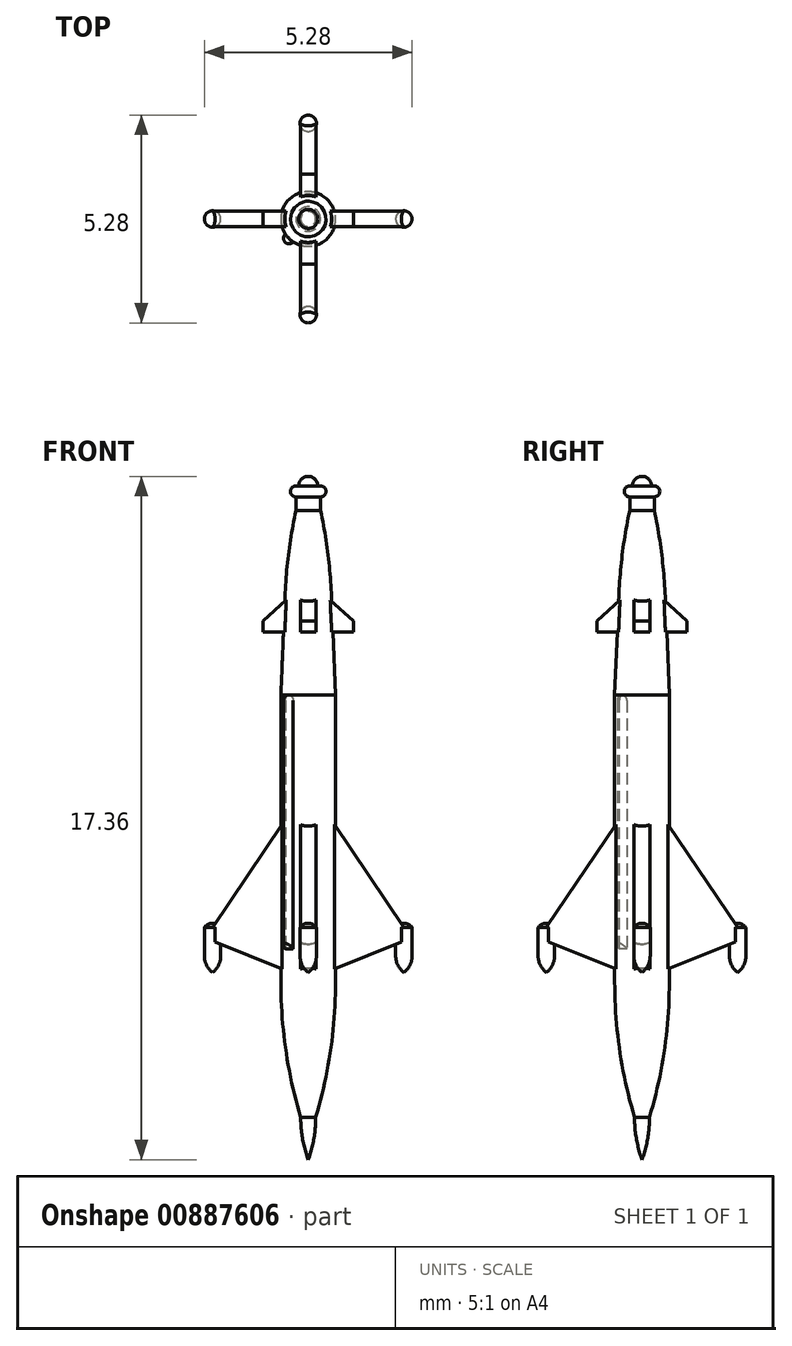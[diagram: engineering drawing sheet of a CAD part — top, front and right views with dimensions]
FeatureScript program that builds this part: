
annotation { "Feature Type Name" : "Feature", "Feature Type Description" : "" }
export const myFeature = defineFeature(function(context is Context, id is Id, definition is map)
    precondition{}
    {
        {
            assignVariable(context, id + "F0", {"name" : "s", "anyValue" : 144});
        }
        {
            var Q0;
            Q0=qCreatedBy(makeId("Front.planeOp"),FACE);
            var sketch = newSketch(context, id + "F1", { "sketchPlane" : qUnion([Q0])});
            skLineSegment(sketch, "E0", {"start": v(0, 0) * mm, "end": v(0, 17.36) * mm});
            skLineSegment(sketch, "E1", {"start": v(0.7, 11.8) * mm, "end": v(0.7, 0) * mm});
            skLineSegment(sketch, "E2", {"start": v(0.7, 0) * mm, "end": v(0, 0) * mm});
            skArc(sketch, "E3", {"start": v(0, 0) * mm, "mid": v(0.14, 0.53) * mm, "end": v(0.2, 1.08) * mm});
            skArc(sketch, "E4", {"start": v(0.2, 1.08) * mm, "mid": v(0.57, 2.78) * mm, "end": v(0.7, 4.51) * mm});
            skLineSegment(sketch, "E5", {"start": v(0.2, 1.08) * mm, "end": v(0.2, 2.11) * mm, "construction": true});
            skArc(sketch, "E6", {"start": v(0.24, 17.12) * mm, "mid": v(0.17, 17.29) * mm, "end": v(0, 17.36) * mm});
            skLineSegment(sketch, "E7", {"start": v(0.24, 17.12) * mm, "end": v(0.31, 17.12) * mm});
            skLineSegment(sketch, "E8", {"start": v(0.31, 16.84) * mm, "end": v(0.31, 16.84) * mm});
            skLineSegment(sketch, "E9", {"start": v(0.31, 16.84) * mm, "end": v(0.31, 16.5) * mm});
            skArc(sketch, "E10", {"start": v(0.31, 16.84) * mm, "mid": v(0.45, 16.98) * mm, "end": v(0.31, 17.12) * mm});
            skLineSegment(sketch, "E11", {"start": v(0.7, 11.8) * mm, "end": v(0.6, 14.3) * mm});
            skArc(sketch, "E12", {"start": v(0.6, 14.3) * mm, "mid": v(0.5, 15.4) * mm, "end": v(0.31, 16.5) * mm});
            skSolve(sketch);
        }
        {
            var Q0;
            {var subQ0=sQuery(id+"F1.wireOp",EDGE,"mrwio9nY-PsAZ-Zbfy-NhIU-sYq0QVbgGXAG");Q0=makeQuery(id+"F1.imprint","IMPRINT",FACE,{"disambiguationData":[TD([[makeQuery(id+"F1.imprint","IMPRINT",EDGE,{"derivedFrom":subQ0}),-1.0]])]});}
            var Q1;
            {var subQ7=sQuery(id+"F1.wireOp",EDGE,"E0");Q1=makeQuery(id+"F1.imprint","IMPRINT",FACE,{"disambiguationData":[TD([[makeQuery(id+"F1.imprint","IMPRINT",EDGE,{"derivedFrom":subQ7}),-1.0]])]});}
            var Q2;
            Q2=sQuery(id+"F1.wireOp",EDGE,"E0");
            revolve(context, id + "F2", {"surfaceOperationType" : NewSurfaceOperationType.NEW, "entities" : qUnion([Q0, Q1]), "axis" : qUnion([Q2]), "revolveType" : RevolveType.FULL});
        }
        {
            var Q0;
            Q0=qCreatedBy(makeId("Front.planeOp"),FACE);
            var sketch = newSketch(context, id + "F3", { "sketchPlane" : qUnion([Q0])});
            skLineSegment(sketch, "E13", {"start": v(0, 0) * mm, "end": v(0, 14.74) * mm});
            skLineSegment(sketch, "E14", {"start": v(0.4, 13.4) * mm, "end": v(0.4, 8.9) * mm});
            skLineSegment(sketch, "E15", {"start": v(0.4, 8.9) * mm, "end": v(2.43, 5.9) * mm});
            skLineSegment(sketch, "E16", {"start": v(0.7, 0) * mm, "end": v(0.7, 32.87) * mm, "construction": true});
            skPoint(sketch, "E17", {"position": v(0.7, 8.47) * mm});
            skLineSegment(sketch, "E18", {"start": v(0.4, 13.4) * mm, "end": v(1.15, 13.4) * mm});
            skLineSegment(sketch, "E19", {"start": v(1.15, 13.4) * mm, "end": v(1.15, 13.68) * mm});
            skLineSegment(sketch, "E20", {"start": v(1.15, 13.68) * mm, "end": v(0, 14.74) * mm});
            skPoint(sketch, "E21", {"position": v(0.7, 13.4) * mm});
            skPoint(sketch, "E22", {"position": v(0.7, 14.1) * mm});
            skLineSegment(sketch, "E23.0", {"start": v(0.7, 4.51) * mm, "end": v(-0.7, 4.51) * mm});
            skLineSegment(sketch, "E24", {"start": v(0, 4.58) * mm, "end": v(2.43, 5.56) * mm});
            skLineSegment(sketch, "E25", {"start": v(2.43, 5.56) * mm, "end": v(2.43, 5.9) * mm});
            skPoint(sketch, "E26", {"position": v(0.7, 4.86) * mm});
            skSolve(sketch);
        }
        {
            var Q0;
            Q0=qSketchRegion(id+"F3",true);
            extrude(context, id + "F4", {"entities" : qUnion([Q0]), "operationType" : NewBodyOperationType.ADD, "depth" : .4 * mm, "offsetDistance" : 25 * mm, "symmetric" : true});
        }
        {
            var Q0;
            Q0=qCreatedBy(makeId("Front.planeOp"),FACE);
            var sketch = newSketch(context, id + "F5", { "sketchPlane" : qUnion([Q0])});
            skLineSegment(sketch, "E27", {"start": v(2.43, 4.76) * mm, "end": v(2.43, 6) * mm});
            skLineSegment(sketch, "E28", {"start": v(2.64, 5.9) * mm, "end": v(2.64, 5.17) * mm});
            skArc(sketch, "E29", {"start": v(2.64, 5.9) * mm, "mid": v(2.55, 5.98) * mm, "end": v(2.43, 6) * mm});
            skArc(sketch, "E30", {"start": v(2.43, 4.76) * mm, "mid": v(2.58, 4.94) * mm, "end": v(2.64, 5.17) * mm});
            skLineSegment(sketch, "E31.0", {"start": v(0.67, 8.52) * mm, "end": v(2.43, 5.9) * mm});
            skSolve(sketch);
        }
        {
            var Q0;
            Q0 = qSketchRegion(id + "F5", true);
            var Q1;
            Q1=sQuery(id+"F5.wireOp",EDGE,"E27");
            revolve(context, id + "F6", {"operationType" : NewBodyOperationType.ADD, "surfaceOperationType" : NewSurfaceOperationType.NEW, "entities" : qUnion([Q0]), "axis" : qUnion([Q1]), "revolveType" : RevolveType.FULL});
        }
        {
            var Q0;
            Q0=makeQuery(id+"F2.opRevolve","SWEPT_BODY",BODY,{"disambiguationData":[OSD([sQuery(id+"F1.wireOp",EDGE,"E0"),sQuery(id+"F1.wireOp",EDGE,"E1"),sQuery(id+"F1.wireOp",EDGE,"E2"),sQuery(id+"F1.wireOp",EDGE,"2EiOItwe-9FNA-eY8p-DkXH-AMy5AHyUmzZA"),sQuery(id+"F1.wireOp",EDGE,"lF35QjYl-MEgV-fRWE-0Yr6-Bt5vS8A7brRf")])]});
            var Q1;
            Q1=makeQuery(id+"F2.opRevolve","SWEPT_FACE",FACE,{"disambiguationData":[OSD([sQuery(id+"F1.wireOp",EDGE,"E1")])]});
            circularPattern(context, id + "F7", {"operationType" : NewBodyOperationType.ADD, "entities" : qUnion([Q0]), "axis" : qUnion([Q1]), "angle" : 360 * degree, "instanceCount" : 4, "equalSpace" : true, "computeTransformsWithoutBuiltin" : true});
        }
        {
            var Q0;
            Q0=qCreatedBy(makeId("Top.planeOp"),FACE);
            cPlane(context, id + "F8", {"entities" : qUnion([Q0]), "cplaneType" : CPlaneType.OFFSET, "offset" : (800 / getVariable(context, 's')) * mm, "width" : 150 * mm, "height" : 150 * mm});
        }
        {
            var Q0;
            Q0=qCreatedBy(id+"F8.planeOp",FACE);
            var sketch = newSketch(context, id + "F9", { "sketchPlane" : qUnion([Q0])});
            skLineSegment(sketch, "E32", {"start": v(-0.06, -0.25) * mm, "end": v(-0.25, -0.06) * mm});
            skLineSegment(sketch, "E33", {"start": v(-0.25, -0.06) * mm, "end": v(-0.59, -0.4) * mm});
            skLineSegment(sketch, "E34", {"start": v(-0.4, -0.59) * mm, "end": v(-0.06, -0.25) * mm});
            skLineSegment(sketch, "E35", {"start": v(0, -0.45) * mm, "end": v(0, 0) * mm, "construction": true});
            skLineSegment(sketch, "E36", {"start": v(0, 0) * mm, "end": v(-0.16, -0.16) * mm, "construction": true});
            skArc(sketch, "E37", {"start": v(-0.59, -0.4) * mm, "mid": v(-0.59, -0.59) * mm, "end": v(-0.4, -0.59) * mm});
            skSolve(sketch);
        }
        {
            var Q0;
            Q0=qSketchRegion(id+"F9",true);
            extrude(context, id + "F10", {"entities" : qUnion([Q0]), "operationType" : NewBodyOperationType.ADD, "depth" : (900 / getVariable(context, 's')) * mm, "offsetDistance" : 25 * mm});
        }
        {
            var Q0;
            Q0=makeQuery(id+"F10.boolean.opBoolean","INTERSECT",EDGE,{"derivedFrom":[makeQuery(id+"F2.opRevolve","SWEPT_FACE",FACE,{"disambiguationData":[OSD([sQuery(id+"F1.wireOp",EDGE,"E1")])]}),makeQuery(id+"F10.opExtrude","CAP_FACE",FACE,{"disambiguationData":[OSD([sQuery(id+"F9.wireOp",EDGE,"E32"),sQuery(id+"F9.wireOp",EDGE,"E33"),sQuery(id+"F9.wireOp",EDGE,"E34"),sQuery(id+"F9.wireOp",EDGE,"E37")])],"isStart":true})]});
            chamfer(context, id + "F11", {"entities" : qUnion([Q0]), "width" : .2 * mm, "tangentPropagation" : true});
        }
        {
            var Q0;
            Q0=makeQuery(id+"F10.opExtrude","CAP_EDGE",EDGE,{"disambiguationData":[OSD([sQuery(id+"F9.wireOp",EDGE,"E37")])],"isStart":false});
            fillet(context, id + "F12", {"entities" : qUnion([Q0]), "radius" : (20 / getVariable(context, 's')) * mm, "tangentPropagation" : true, "allowEdgeOverflow" : false});
        }
    });
